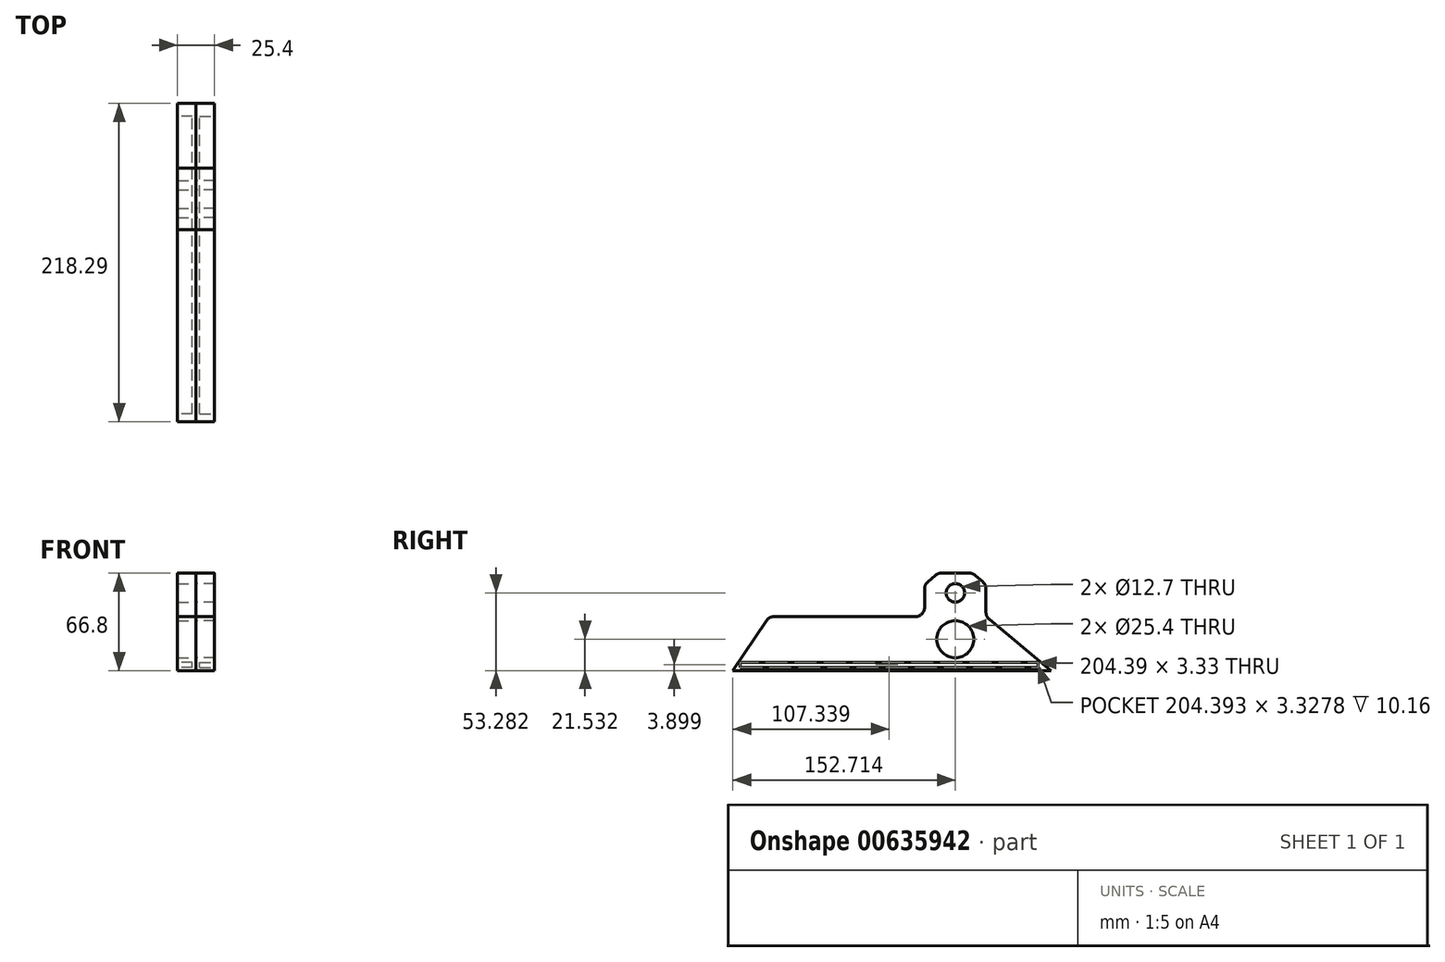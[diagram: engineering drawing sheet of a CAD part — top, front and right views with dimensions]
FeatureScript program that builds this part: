
annotation { "Feature Type Name" : "Feature", "Feature Type Description" : "" }
export const myFeature = defineFeature(function(context is Context, id is Id, definition is map)
    precondition{}
    {
        {
            var Q0;
            Q0=qCreatedBy(makeId("Right.planeOp"),FACE);
            var sketch = newSketch(context, id + "F0", { "sketchPlane" : qUnion([Q0])});
            skLineSegment(sketch, "E0", {"start": v(-110.54, 0) * mm, "end": v(-87.38, 34.19) * mm});
            skLineSegment(sketch, "E1", {"start": v(-82.12, 36.98) * mm, "end": v(14.72, 36.98) * mm});
            skLineSegment(sketch, "E2", {"start": v(21.07, 43.33) * mm, "end": v(21.07, 55.95) * mm});
            skLineSegment(sketch, "E3", {"start": v(23.26, 60.74) * mm, "end": v(28.43, 65.24) * mm});
            skLineSegment(sketch, "E4", {"start": v(32.6, 66.8) * mm, "end": v(51.74, 66.8) * mm});
            skLineSegment(sketch, "E5", {"start": v(55.92, 65.23) * mm, "end": v(61.05, 60.74) * mm});
            skLineSegment(sketch, "E6", {"start": v(63.22, 55.96) * mm, "end": v(63.22, 39.96) * mm});
            skLineSegment(sketch, "E7", {"start": v(65.51, 35.07) * mm, "end": v(107.75, 0) * mm});
            skLineSegment(sketch, "E8", {"start": v(107.75, 0) * mm, "end": v(-110.54, 0) * mm});
            skCircle(sketch, "E9", {"center": v(42.17, 53.28) * mm, "radius": 6.35 * mm});
            skPoint(sketch, "E9.centerSnap0", {"position": v(42.17, 66.8) * mm});
            skCircle(sketch, "E10", {"center": v(42.17, 21.53) * mm, "radius": 12.7 * mm});
            skPoint(sketch, "E11.visualSharp", {"position": v(-85.49, 36.98) * mm});
            skArc(sketch, "E11.filletArc", {"start": v(-82.12, 36.98) * mm, "mid": v(-85.1, 36.24) * mm, "end": v(-87.38, 34.19) * mm});
            skPoint(sketch, "E12.visualSharp", {"position": v(21.07, 36.98) * mm});
            skArc(sketch, "E12.filletArc", {"start": v(14.72, 36.98) * mm, "mid": v(19.21, 38.84) * mm, "end": v(21.07, 43.33) * mm});
            skPoint(sketch, "E13.visualSharp", {"position": v(63.22, 36.98) * mm});
            skArc(sketch, "E13.filletArc", {"start": v(63.22, 39.96) * mm, "mid": v(63.82, 37.26) * mm, "end": v(65.51, 35.07) * mm});
            skPoint(sketch, "E14.visualSharp", {"position": v(21.07, 58.85) * mm});
            skArc(sketch, "E14.filletArc", {"start": v(23.26, 60.74) * mm, "mid": v(21.64, 58.59) * mm, "end": v(21.07, 55.95) * mm});
            skPoint(sketch, "E15.visualSharp", {"position": v(30.22, 66.8) * mm});
            skArc(sketch, "E15.filletArc", {"start": v(32.6, 66.8) * mm, "mid": v(30.37, 66.4) * mm, "end": v(28.43, 65.24) * mm});
            skPoint(sketch, "E16.visualSharp", {"position": v(54.13, 66.8) * mm});
            skArc(sketch, "E16.filletArc", {"start": v(55.92, 65.23) * mm, "mid": v(53.98, 66.4) * mm, "end": v(51.74, 66.8) * mm});
            skPoint(sketch, "E17.visualSharp", {"position": v(63.22, 58.85) * mm});
            skArc(sketch, "E17.filletArc", {"start": v(63.22, 55.96) * mm, "mid": v(62.65, 58.59) * mm, "end": v(61.05, 60.74) * mm});
            skSolve(sketch);
        }
        {
            var Q0;
            Q0 = qSketchRegion(id + "F0", true);
            extrude(context, id + "F1", {"entities" : qUnion([Q0]), "depth" : 12.7 * mm, "offsetDistance" : 25.4 * mm});
        }
        {
            var Q0;
            Q0=makeQuery(id+"F1.opExtrude","CAP_FACE",FACE,{"disambiguationData":[OSD([sQuery(id+"F0.wireOp",EDGE,"E0"),sQuery(id+"F0.wireOp",EDGE,"E1"),sQuery(id+"F0.wireOp",EDGE,"E2"),sQuery(id+"F0.wireOp",EDGE,"E3"),sQuery(id+"F0.wireOp",EDGE,"E4"),sQuery(id+"F0.wireOp",EDGE,"E5"),sQuery(id+"F0.wireOp",EDGE,"E6"),sQuery(id+"F0.wireOp",EDGE,"E7"),sQuery(id+"F0.wireOp",EDGE,"E8"),sQuery(id+"F0.wireOp",EDGE,"E9"),sQuery(id+"F0.wireOp",EDGE,"E10"),sQuery(id+"F0.wireOp",EDGE,"E11.filletArc"),sQuery(id+"F0.wireOp",EDGE,"E12.filletArc"),sQuery(id+"F0.wireOp",EDGE,"E13.filletArc"),sQuery(id+"F0.wireOp",EDGE,"E14.filletArc"),sQuery(id+"F0.wireOp",EDGE,"E15.filletArc"),sQuery(id+"F0.wireOp",EDGE,"E16.filletArc"),sQuery(id+"F0.wireOp",EDGE,"E17.filletArc")])],"isStart":false});
            var sketch = newSketch(context, id + "F2", { "sketchPlane" : qUnion([Q0])});
            skLineSegment(sketch, "E18", {"start": v(-105.4, 5.56) * mm, "end": v(99, 5.56) * mm});
            skLineSegment(sketch, "E19", {"start": v(99, 5.56) * mm, "end": v(99, 2.24) * mm});
            skLineSegment(sketch, "E20", {"start": v(99, 2.24) * mm, "end": v(-105.4, 2.24) * mm});
            skLineSegment(sketch, "E21", {"start": v(-105.4, 2.24) * mm, "end": v(-105.4, 5.56) * mm});
            skSolve(sketch);
        }
        {
            var Q0;
            Q0 = qSketchRegion(id + "F2", true);
            extrude(context, id + "F3", {"entities" : qUnion([Q0]), "operationType" : NewBodyOperationType.REMOVE, "oppositeDirection" : true, "depth" : 10.16 * mm, "offsetDistance" : 25.4 * mm});
        }
        {
            var Q0;
            Q0=makeQuery(id+"F1.opExtrude","SWEPT_BODY",BODY,{"disambiguationData":[OSD([sQuery(id+"F0.wireOp",EDGE,"E0"),sQuery(id+"F0.wireOp",EDGE,"E1"),sQuery(id+"F0.wireOp",EDGE,"E2"),sQuery(id+"F0.wireOp",EDGE,"E3"),sQuery(id+"F0.wireOp",EDGE,"E4"),sQuery(id+"F0.wireOp",EDGE,"E5"),sQuery(id+"F0.wireOp",EDGE,"E6"),sQuery(id+"F0.wireOp",EDGE,"E7"),sQuery(id+"F0.wireOp",EDGE,"E8"),sQuery(id+"F0.wireOp",EDGE,"E9"),sQuery(id+"F0.wireOp",EDGE,"E10"),sQuery(id+"F0.wireOp",EDGE,"E11.filletArc"),sQuery(id+"F0.wireOp",EDGE,"E12.filletArc"),sQuery(id+"F0.wireOp",EDGE,"E13.filletArc"),sQuery(id+"F0.wireOp",EDGE,"E14.filletArc"),sQuery(id+"F0.wireOp",EDGE,"E15.filletArc"),sQuery(id+"F0.wireOp",EDGE,"E16.filletArc"),sQuery(id+"F0.wireOp",EDGE,"E17.filletArc")])]});
            var Q1;
            Q1=makeQuery(id+"F1.opExtrude","CAP_FACE",FACE,{"disambiguationData":[OSD([sQuery(id+"F0.wireOp",EDGE,"E0"),sQuery(id+"F0.wireOp",EDGE,"E1"),sQuery(id+"F0.wireOp",EDGE,"E2"),sQuery(id+"F0.wireOp",EDGE,"E3"),sQuery(id+"F0.wireOp",EDGE,"E4"),sQuery(id+"F0.wireOp",EDGE,"E5"),sQuery(id+"F0.wireOp",EDGE,"E6"),sQuery(id+"F0.wireOp",EDGE,"E7"),sQuery(id+"F0.wireOp",EDGE,"E8"),sQuery(id+"F0.wireOp",EDGE,"E9"),sQuery(id+"F0.wireOp",EDGE,"E10"),sQuery(id+"F0.wireOp",EDGE,"E11.filletArc"),sQuery(id+"F0.wireOp",EDGE,"E12.filletArc"),sQuery(id+"F0.wireOp",EDGE,"E13.filletArc"),sQuery(id+"F0.wireOp",EDGE,"E14.filletArc"),sQuery(id+"F0.wireOp",EDGE,"E15.filletArc"),sQuery(id+"F0.wireOp",EDGE,"E16.filletArc"),sQuery(id+"F0.wireOp",EDGE,"E17.filletArc")])],"isStart":true});
            mirror(context, id + "F4", {"entities" : qUnion([Q0]), "mirrorPlane" : qUnion([Q1])});
        }
    });
